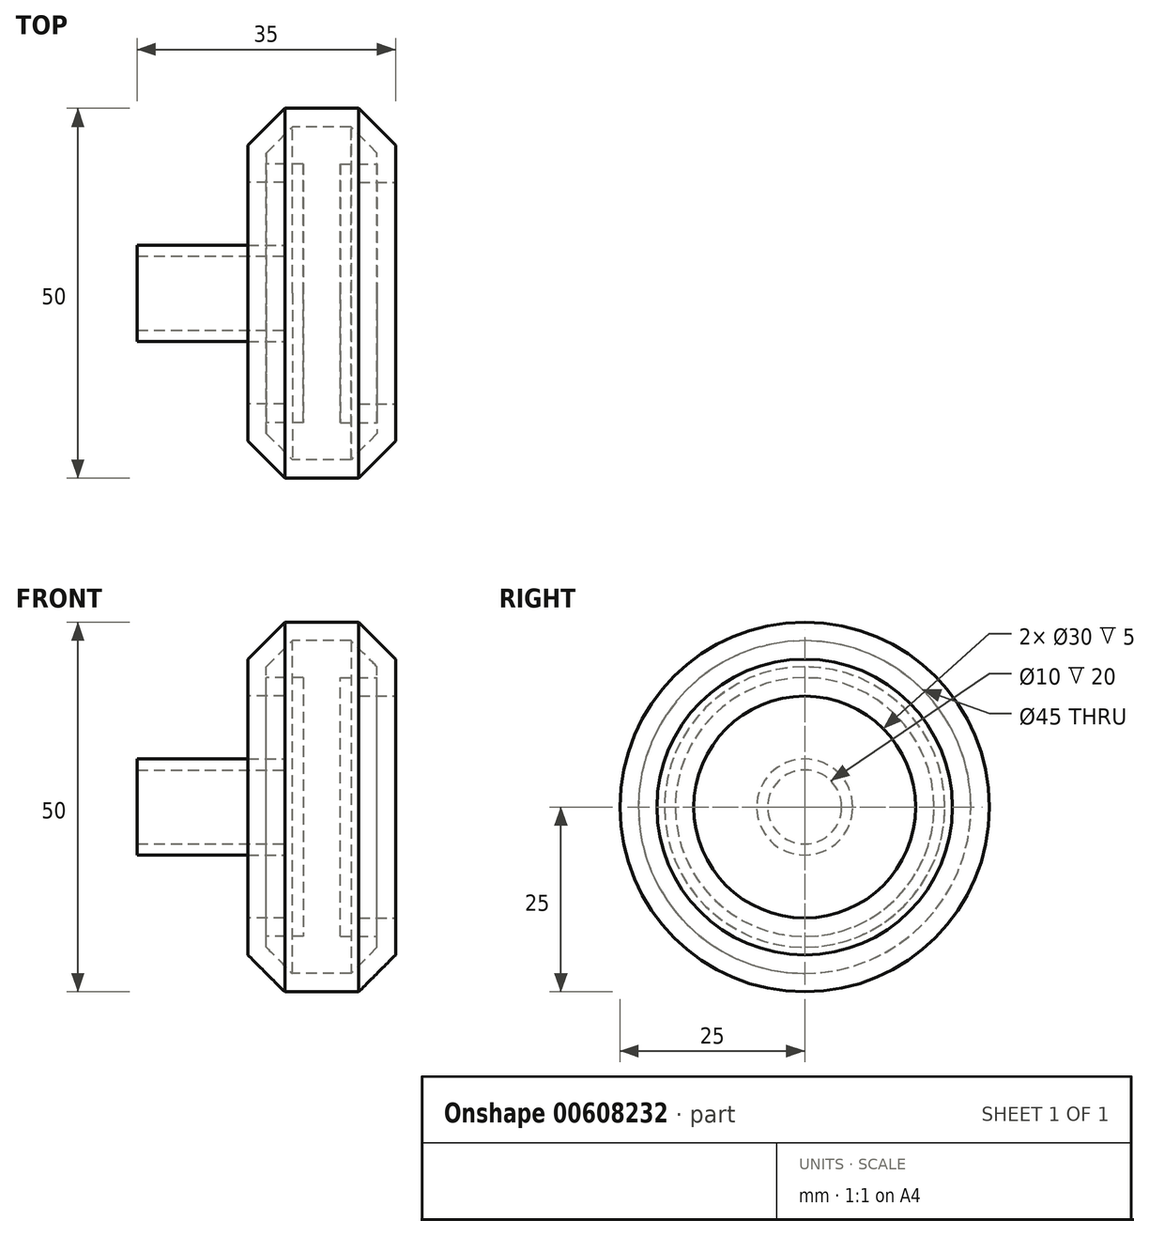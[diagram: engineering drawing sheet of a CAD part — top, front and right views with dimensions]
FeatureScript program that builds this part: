
annotation { "Feature Type Name" : "Feature", "Feature Type Description" : "" }
export const myFeature = defineFeature(function(context is Context, id is Id, definition is map)
    precondition{}
    {
        {
            var Q0;
            Q0=qCreatedBy(makeId("Right.planeOp"),FACE);
            var sketch = newSketch(context, id + "F0", { "sketchPlane" : qUnion([Q0])});
            skCircle(sketch, "E0", {"center": v(0, 0) * mm, "radius": 25 * mm});
            skSolve(sketch);
        }
        {
            var Q0;
            Q0=makeQuery(id+"F0.imprint","IMPRINT",FACE,{"disambiguationData":[TD([[makeQuery(id+"F0.imprint","IMPRINT",EDGE,{"derivedFrom":sQuery(id+"F0.wireOp",EDGE,"E0")}),1.0]])]});
            extrude(context, id + "F1", {"entities" : qUnion([Q0]), "depth" : 20 * mm, "offsetDistance" : 25 * mm});
        }
        {
            var Q0;
            Q0=makeQuery(id+"F1.opExtrude","CAP_FACE",FACE,{"disambiguationData":[OSD([sQuery(id+"F0.wireOp",EDGE,"E0")])],"isStart":false});
            chamfer(context, id + "F2", {"entities" : qUnion([Q0]), "width" : 5 * mm, "tangentPropagation" : true});
        }
        {
            var Q0;
            Q0=makeQuery(id+"F1.opExtrude","CAP_FACE",FACE,{"disambiguationData":[OSD([sQuery(id+"F0.wireOp",EDGE,"E0")])],"isStart":true});
            chamfer(context, id + "F3", {"entities" : qUnion([Q0]), "width" : 5 * mm, "tangentPropagation" : true});
        }
        {
            var Q0;
            Q0=makeQuery(id+"F1.opExtrude","CAP_FACE",FACE,{"disambiguationData":[OSD([sQuery(id+"F0.wireOp",EDGE,"E0")])],"isStart":true});
            var sketch = newSketch(context, id + "F4", { "sketchPlane" : qUnion([Q0])});
            skCircle(sketch, "E1", {"center": v(0, 0) * mm, "radius": 15 * mm});
            skSolve(sketch);
        }
        {
            var Q0;
            Q0=qSketchRegion(id+"F4",true);
            extrude(context, id + "F5", {"entities" : qUnion([Q0]), "operationType" : NewBodyOperationType.REMOVE, "oppositeDirection" : true, "depth" : 5 * mm, "offsetDistance" : 25 * mm});
        }
        {
            var Q0;
            Q0=makeQuery(id+"F1.opExtrude","CAP_FACE",FACE,{"disambiguationData":[OSD([sQuery(id+"F0.wireOp",EDGE,"E0")])],"isStart":false});
            var sketch = newSketch(context, id + "F6", { "sketchPlane" : qUnion([Q0])});
            skCircle(sketch, "E2", {"center": v(0, 0) * mm, "radius": 15 * mm});
            skSolve(sketch);
        }
        {
            var Q0;
            Q0=qSketchRegion(id+"F6",true);
            extrude(context, id + "F7", {"entities" : qUnion([Q0]), "operationType" : NewBodyOperationType.REMOVE, "oppositeDirection" : true, "depth" : 5 * mm, "offsetDistance" : 25 * mm});
        }
        {
            var Q0;
            Q0=makeQuery(id+"F5.boolean.opBoolean","COPY",FACE,{"derivedFrom":makeQuery(id+"F5.opExtrude","CAP_FACE",FACE,{"disambiguationData":[OSD([sQuery(id+"F4.wireOp",EDGE,"E1")])],"isStart":false})});
            var sketch = newSketch(context, id + "F8", { "sketchPlane" : qUnion([Q0])});
            skCircle(sketch, "E3", {"center": v(0, 0) * mm, "radius": 5 * mm});
            skCircle(sketch, "E4", {"center": v(0, 0) * mm, "radius": 6.5 * mm});
            skSolve(sketch);
        }
        {
            var Q0;
            Q0=qSketchRegion(id+"F8",true);
            extrude(context, id + "F9", {"entities" : qUnion([Q0]), "operationType" : NewBodyOperationType.ADD, "depth" : 20 * mm, "offsetDistance" : 25 * mm});
        }
        {
            var Q0;
            Q0=makeQuery(id+"F9.opExtrude","CAP_FACE",FACE,{"disambiguationData":[OSD([sQuery(id+"F8.wireOp",EDGE,"E3"),sQuery(id+"F8.wireOp",EDGE,"E4")])],"isStart":false});
            shell(context, id + "F10", {"entities" : qUnion([Q0]), "thickness" : 2.5 * mm});
        }
    });
